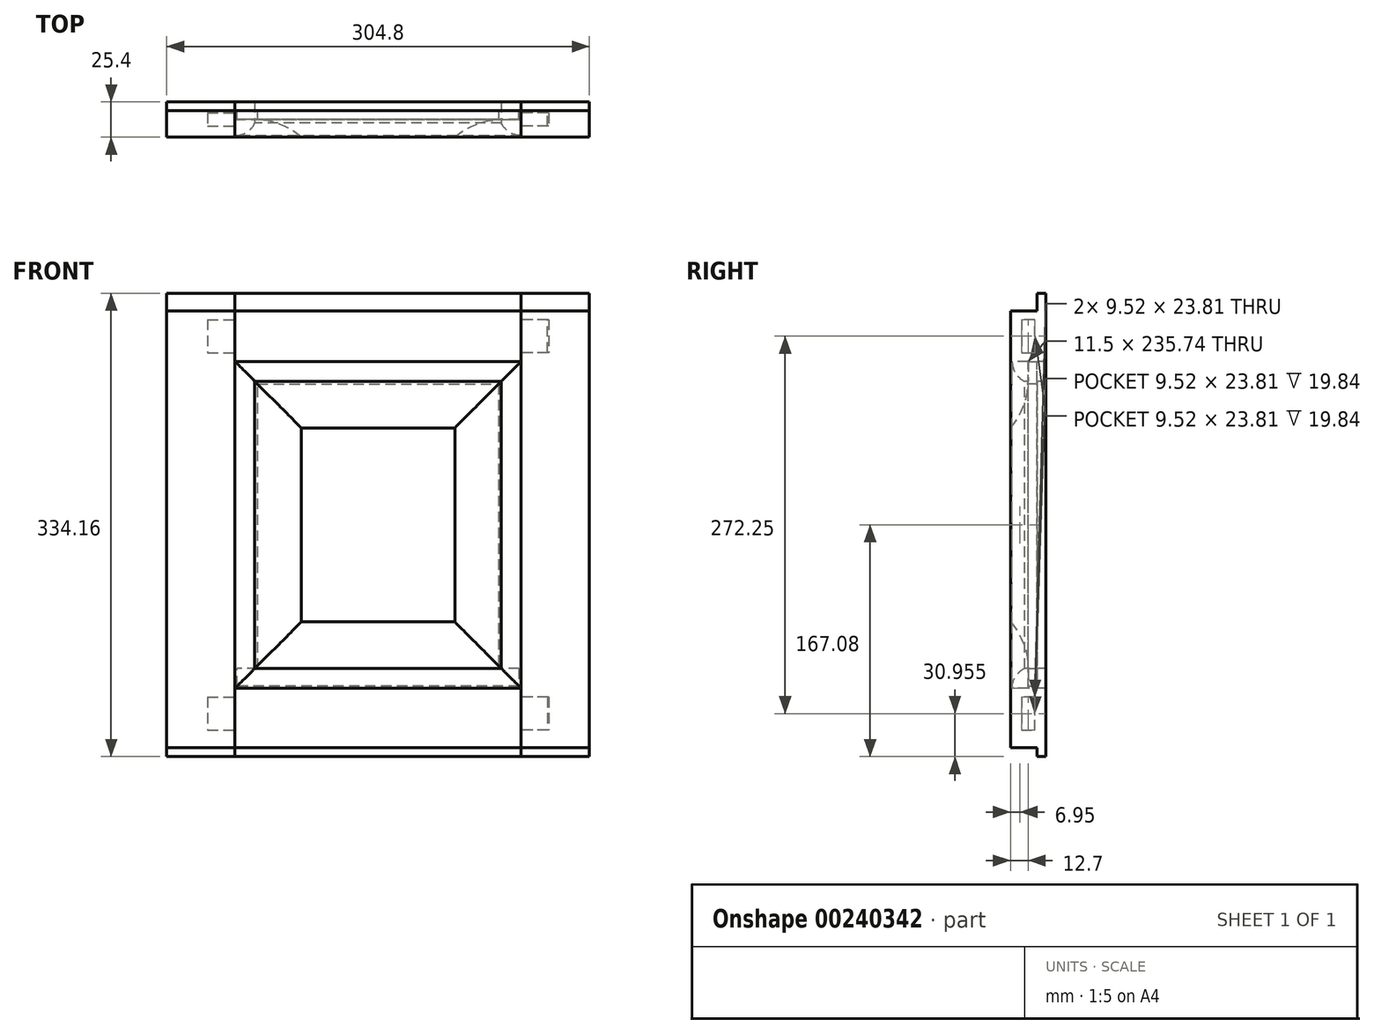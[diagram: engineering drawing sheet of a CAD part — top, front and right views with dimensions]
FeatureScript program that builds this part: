
annotation { "Feature Type Name" : "Feature", "Feature Type Description" : "" }
export const myFeature = defineFeature(function(context is Context, id is Id, definition is map)
    precondition{}
    {
        {
            var Q0;
            Q0=qCreatedBy(makeId("Front.planeOp"),FACE);
            var sketch = newSketch(context, id + "F0", { "sketchPlane" : qUnion([Q0])});
            skLineSegment(sketch, "E0.bottom", {"start": v(88.9, 103.58) * mm, "end": v(-88.9, 103.58) * mm});
            skLineSegment(sketch, "E1", {"start": v(-88.9, 103.58) * mm, "end": v(-103.19, 117.87) * mm});
            skLineSegment(sketch, "E2", {"start": v(-103.19, 117.87) * mm, "end": v(-103.19, 167.08) * mm});
            skLineSegment(sketch, "E3", {"start": v(-103.19, 167.08) * mm, "end": v(111.13, 167.08) * mm});
            skLineSegment(sketch, "E4.MirrorCS", {"start": v(-88.9, -103.58) * mm, "end": v(-103.19, -117.87) * mm});
            skLineSegment(sketch, "E5.MirrorCS", {"start": v(88.9, -103.58) * mm, "end": v(-88.9, -103.58) * mm});
            skLineSegment(sketch, "E6.MirrorCS", {"start": v(-103.19, -167.08) * mm, "end": v(111.13, -167.08) * mm});
            skLineSegment(sketch, "E7.MirrorCS", {"start": v(-103.19, -117.87) * mm, "end": v(-103.19, -167.08) * mm});
            skLineSegment(sketch, "E8", {"start": v(-103.19, 167.08) * mm, "end": v(-152.4, 167.08) * mm});
            skLineSegment(sketch, "E9", {"start": v(-152.4, 167.08) * mm, "end": v(-152.4, -167.08) * mm});
            skLineSegment(sketch, "E10", {"start": v(-152.4, -167.08) * mm, "end": v(-103.19, -167.08) * mm});
            skLineSegment(sketch, "E11", {"start": v(-88.9, 103.58) * mm, "end": v(-88.9, -103.58) * mm});
            skLineSegment(sketch, "E12.MirrorCS", {"start": v(88.9, -103.58) * mm, "end": v(103.19, -117.87) * mm});
            skLineSegment(sketch, "E13.MirrorCS", {"start": v(103.19, 117.87) * mm, "end": v(103.19, 167.08) * mm});
            skLineSegment(sketch, "E14.MirrorCS", {"start": v(103.19, -117.87) * mm, "end": v(103.19, -167.08) * mm});
            skLineSegment(sketch, "E15.MirrorCS", {"start": v(152.4, 167.08) * mm, "end": v(152.4, -167.08) * mm});
            skLineSegment(sketch, "E16.MirrorCS", {"start": v(152.4, -167.08) * mm, "end": v(103.19, -167.08) * mm});
            skLineSegment(sketch, "E17.MirrorCS", {"start": v(103.19, 167.08) * mm, "end": v(152.4, 167.08) * mm});
            skLineSegment(sketch, "E18.MirrorCS", {"start": v(88.9, 103.58) * mm, "end": v(88.9, -103.58) * mm});
            skLineSegment(sketch, "E19", {"start": v(88.9, 103.58) * mm, "end": v(103.19, 117.87) * mm});
            skSolve(sketch);
        }
        {
            var Q0;
            Q0=makeQuery(id+"F0.imprint","IMPRINT",FACE,{"disambiguationData":[TD([[makeQuery(id+"F0.imprint","IMPRINT",EDGE,{"derivedFrom":sQuery(id+"F0.wireOp",EDGE,"E0.bottom")}),-1.0]])]});
            extrude(context, id + "F1", {"entities" : qUnion([Q0]), "oppositeDirection" : true, "depth" : 25.4 * mm});
        }
        {
            var Q0;
            Q0=makeQuery(id+"F1.opExtrude","SWEPT_FACE",FACE,{"disambiguationData":[OSD([sQuery(id+"F0.wireOp",EDGE,"E2")])]});
            var sketch = newSketch(context, id + "F2", { "sketchPlane" : qUnion([Q0])});
            skLineSegment(sketch, "E20.bottom", {"start": v(-7.94, 124.22) * mm, "end": v(-17.46, 124.22) * mm});
            skLineSegment(sketch, "E20.top", {"start": v(-7.94, 148.03) * mm, "end": v(-17.46, 148.03) * mm});
            skLineSegment(sketch, "E20.left", {"start": v(-7.94, 124.22) * mm, "end": v(-7.94, 148.03) * mm});
            skLineSegment(sketch, "E20.right", {"start": v(-17.46, 124.22) * mm, "end": v(-17.46, 148.03) * mm});
            skPoint(sketch, "E20.middle", {"position": v(-12.7, 136.13) * mm});
            skSolve(sketch);
        }
        {
            var Q0;
            Q0 = qSketchRegion(id + "F2", true);
            extrude(context, id + "F3", {"entities" : qUnion([Q0]), "depth" : 19.05 * mm});
        }
        {
            var Q0;
            Q0=makeQuery(id+"F3.opExtrude","SWEPT_BODY",BODY,{"disambiguationData":[OSD([sQuery(id+"F2.wireOp",EDGE,"E20.bottom"),sQuery(id+"F2.wireOp",EDGE,"E20.top"),sQuery(id+"F2.wireOp",EDGE,"E20.left"),sQuery(id+"F2.wireOp",EDGE,"E20.right")])]});
            var Q1;
            Q1=qCreatedBy(makeId("Right.planeOp"),FACE);
            mirror(context, id + "F4", {"operationType" : NewBodyOperationType.ADD, "entities" : qUnion([Q0]), "mirrorPlane" : qUnion([Q1])});
        }
        {
            var Q0;
            Q0=makeQuery(id+"F0.imprint","IMPRINT",FACE,{"disambiguationData":[TD([[makeQuery(id+"F0.imprint","IMPRINT",EDGE,{"derivedFrom":sQuery(id+"F0.wireOp",EDGE,"E1")}),1.0]])]});
            extrude(context, id + "F5", {"entities" : qUnion([Q0]), "oppositeDirection" : true, "depth" : 25.4 * mm});
        }
        {
            var Q0;
            Q0=makeQuery(id+"F1.opExtrude","SWEPT_BODY",BODY,{"disambiguationData":[OSD([sQuery(id+"F0.wireOp",EDGE,"E0.bottom"),sQuery(id+"F0.wireOp",EDGE,"E1"),sQuery(id+"F0.wireOp",EDGE,"E2"),sQuery(id+"F0.wireOp",EDGE,"E3"),sQuery(id+"F0.wireOp",EDGE,"6457b620-730b-450c-8f20-c046bc1b6dd80.MirrorCS"),sQuery(id+"F0.wireOp",EDGE,"E13.MirrorCS")])]});
            var Q1;
            Q1=qCreatedBy(makeId("Top.planeOp"),FACE);
            mirror(context, id + "F6", {"entities" : qUnion([Q0]), "mirrorPlane" : qUnion([Q1])});
        }
        {
            var Q0;
            Q0=makeQuery(id+"F5.opExtrude","SWEPT_FACE",FACE,{"disambiguationData":[OSD([sQuery(id+"F0.wireOp",EDGE,"E11")])]});
            var sketch = newSketch(context, id + "F7", { "sketchPlane" : qUnion([Q0])});
            skLineSegment(sketch, "E21.0", {"start": v(19.05, 117.87) * mm, "end": v(19.05, -117.87) * mm});
            skLineSegment(sketch, "E22.0", {"start": v(19.05, 117.87) * mm, "end": v(12.7, 117.87) * mm});
            skLineSegment(sketch, "E23.0", {"start": v(19.05, -117.87) * mm, "end": v(12.7, -117.87) * mm});
            skLineSegment(sketch, "E24", {"start": v(12.7, -117.87) * mm, "end": v(12.7, 117.87) * mm});
            skSolve(sketch);
        }
        {
            var Q0;
            Q0=makeQuery(id+"F5.opExtrude","SWEPT_FACE",FACE,{"disambiguationData":[OSD([sQuery(id+"F0.wireOp",EDGE,"E7.MirrorCS")])]});
            var sketch = newSketch(context, id + "F8", { "sketchPlane" : qUnion([Q0])});
            skLineSegment(sketch, "E25.0.0", {"start": v(7.94, 148.03) * mm, "end": v(7.94, 124.22) * mm});
            skLineSegment(sketch, "E25.0.1", {"start": v(7.94, 124.22) * mm, "end": v(17.46, 124.22) * mm});
            skLineSegment(sketch, "E25.0.2", {"start": v(17.46, 124.22) * mm, "end": v(17.46, 148.03) * mm});
            skLineSegment(sketch, "E25.0.3", {"start": v(17.46, 148.03) * mm, "end": v(7.94, 148.03) * mm});
            skLineSegment(sketch, "E26.0.0", {"start": v(7.94, -124.22) * mm, "end": v(7.94, -148.03) * mm});
            skLineSegment(sketch, "E26.0.1", {"start": v(7.94, -148.03) * mm, "end": v(17.46, -148.03) * mm});
            skLineSegment(sketch, "E26.0.2", {"start": v(17.46, -148.03) * mm, "end": v(17.46, -124.22) * mm});
            skLineSegment(sketch, "E26.0.3", {"start": v(17.46, -124.22) * mm, "end": v(7.94, -124.22) * mm});
            skSolve(sketch);
        }
        {
            var Q0;
            Q0 = qSketchRegion(id + "F8", true);
            extrude(context, id + "F9", {"entities" : qUnion([Q0]), "operationType" : NewBodyOperationType.REMOVE, "oppositeDirection" : true, "depth" : 19.84 * mm});
        }
        {
            var Q0;
            Q0=qCreatedBy(makeId("Top.planeOp"),FACE);
            var sketch = newSketch(context, id + "F10", { "sketchPlane" : qUnion([Q0])});
            skLineSegment(sketch, "E27.0", {"start": v(-86.89, 19.05) * mm, "end": v(-103.19, 19.05) * mm});
            skLineSegment(sketch, "E28", {"start": v(-103.19, 19.05) * mm, "end": v(-103.19, 12.7) * mm});
            skPoint(sketch, "E28.startSnap0", {"position": v(-92.07, 19.05) * mm});
            skLineSegment(sketch, "E29", {"start": v(-103.19, 12.7) * mm, "end": v(-86.89, 12.7) * mm});
            skLineSegment(sketch, "E30", {"start": v(-86.89, 12.7) * mm, "end": v(-86.89, 19.05) * mm});
            skPoint(sketch, "E31.orphan", {"position": v(-95.25, 19.05) * mm});
            skPoint(sketch, "E32.orphan", {"position": v(-88.9, 19.05) * mm});
            skSolve(sketch);
        }
        {
            var Q0;
            Q0 = qSketchRegion(id + "F10", true);
            var Q1;
            Q1=makeQuery(id+"F5.opExtrude","SWEPT_FACE",FACE,{"disambiguationData":[OSD([sQuery(id+"F0.wireOp",EDGE,"E4.MirrorCS")])]});
            extrude(context, id + "F11", {"entities" : qUnion([Q0]), "operationType" : NewBodyOperationType.REMOVE, "endBound" : BoundingType.UP_TO_SURFACE, "oppositeDirection" : true, "endBoundEntityFace" : qUnion([Q1]), "depth" : 25.4 * mm});
        }
        {
            var Q0;
            Q0=makeQuery(id+"F5.opExtrude","SWEPT_BODY",BODY,{"disambiguationData":[OSD([sQuery(id+"F0.wireOp",EDGE,"E1"),sQuery(id+"F0.wireOp",EDGE,"E2"),sQuery(id+"F0.wireOp",EDGE,"E4.MirrorCS"),sQuery(id+"F0.wireOp",EDGE,"E7.MirrorCS"),sQuery(id+"F0.wireOp",EDGE,"E8"),sQuery(id+"F0.wireOp",EDGE,"E9"),sQuery(id+"F0.wireOp",EDGE,"E10"),sQuery(id+"F0.wireOp",EDGE,"E11")])]});
            var Q1;
            Q1=qCreatedBy(makeId("Right.planeOp"),FACE);
            mirror(context, id + "F12", {"entities" : qUnion([Q0]), "mirrorPlane" : qUnion([Q1])});
        }
        {
            var Q0;
            Q0=qCreatedBy(makeId("Top.planeOp"),FACE);
            var sketch = newSketch(context, id + "F13", { "sketchPlane" : qUnion([Q0])});
            skLineSegment(sketch, "E33.0", {"start": v(-88.9, -0.4) * mm, "end": v(-103.19, -0.4) * mm});
            skLineSegment(sketch, "E34.0", {"start": v(-103.19, 19.05) * mm, "end": v(-103.19, -0.4) * mm});
            skPoint(sketch, "E35.orphan", {"position": v(-103.19, 12.7) * mm});
            skLineSegment(sketch, "E36.0", {"start": v(-88.9, 12.7) * mm, "end": v(-88.9, -0.4) * mm});
            skPoint(sketch, "E37.orphan", {"position": v(-88.9, 0) * mm});
            skLineSegment(sketch, "E38", {"start": v(-103.19, 1.2) * mm, "end": v(-106.37, 1.2) * mm, "construction": true});
            skArc(sketch, "E39", {"start": v(-103.19, 1.2) * mm, "mid": v(-94.76, 3.61) * mm, "end": v(-88.9, 10.15) * mm});
            skSolve(sketch);
        }
        {
            var Q0;
            Q0 = qSketchRegion(id + "F13", true);
            var Q1;
            Q1=makeQuery(id+"F5.opExtrude","CAP_EDGE",EDGE,{"disambiguationData":[OSD([sQuery(id+"F0.wireOp",EDGE,"E11")])],"isStart":true});
            var Q2;
            Q2=makeQuery(id+"F1.opExtrude","CAP_EDGE",EDGE,{"disambiguationData":[OSD([sQuery(id+"F0.wireOp",EDGE,"E0.bottom")])],"isStart":true});
            var Q3;
            Q3=makeQuery(id+"F12.opPattern","COPY",EDGE,{"derivedFrom":makeQuery(id+"F5.opExtrude","CAP_EDGE",EDGE,{"disambiguationData":[OSD([sQuery(id+"F0.wireOp",EDGE,"E11")])],"isStart":true}),"instanceName":"1"});
            var Q4;
            Q4=makeQuery(id+"F6.opPattern","COPY",EDGE,{"derivedFrom":makeQuery(id+"F1.opExtrude","CAP_EDGE",EDGE,{"disambiguationData":[OSD([sQuery(id+"F0.wireOp",EDGE,"E0.bottom")])],"isStart":true}),"instanceName":"1"});
            sweep(context, id + "F14", {"operationType" : NewBodyOperationType.REMOVE, "profiles" : qUnion([Q0]), "path" : qUnion([Q1, Q2, Q3, Q4])});
        }
        {
            var Q0;
            Q0=qCreatedBy(makeId("Top.planeOp"),FACE);
            var sketch = newSketch(context, id + "F15", { "sketchPlane" : qUnion([Q0])});
            skLineSegment(sketch, "E40", {"start": v(-55.3, 0) * mm, "end": v(0, 0) * mm});
            skLineSegment(sketch, "E41.0", {"start": v(-101.6, 19.05) * mm, "end": v(-101.6, 12.7) * mm});
            skLineSegment(sketch, "E42.0", {"start": v(-88.9, 12.7) * mm, "end": v(-101.6, 12.7) * mm});
            skArc(sketch, "E43", {"start": v(-88.9, 12.7) * mm, "mid": v(-70.94, 9.42) * mm, "end": v(-55.3, 0) * mm});
            skLineSegment(sketch, "E44.0", {"start": v(-88.9, 19.05) * mm, "end": v(0, 19.05) * mm});
            skPoint(sketch, "E45.orphan", {"position": v(-101.6, 19.05) * mm});
            skLineSegment(sketch, "E46.0", {"start": v(-101.6, 19.05) * mm, "end": v(-88.9, 19.05) * mm});
            skLineSegment(sketch, "E47", {"start": v(0, 0) * mm, "end": v(0, 19.05) * mm});
            skSolve(sketch);
        }
        {
            var Q0;
            Q0 = qSketchRegion(id + "F15", true);
            var Q1;
            Q1=makeQuery(id+"F5.opExtrude","CAP_EDGE",EDGE,{"disambiguationData":[OSD([sQuery(id+"F0.wireOp",EDGE,"E11")])],"isStart":false});
            var Q2;
            Q2=makeQuery(id+"F1.opExtrude","CAP_EDGE",EDGE,{"disambiguationData":[OSD([sQuery(id+"F0.wireOp",EDGE,"E0.bottom")])],"isStart":false});
            var Q3;
            Q3=makeQuery(id+"F12.opPattern","COPY",EDGE,{"derivedFrom":makeQuery(id+"F5.opExtrude","CAP_EDGE",EDGE,{"disambiguationData":[OSD([sQuery(id+"F0.wireOp",EDGE,"E11")])],"isStart":false}),"instanceName":"1"});
            var Q4;
            Q4=makeQuery(id+"F6.opPattern","COPY",EDGE,{"derivedFrom":makeQuery(id+"F1.opExtrude","CAP_EDGE",EDGE,{"disambiguationData":[OSD([sQuery(id+"F0.wireOp",EDGE,"E0.bottom")])],"isStart":false}),"instanceName":"1"});
            sweep(context, id + "F16", {"profiles" : qUnion([Q0]), "path" : qUnion([Q1, Q2, Q3, Q4])});
        }
        {
            var Q0;
            Q0=makeQuery(id+"F1.opExtrude","SWEPT_FACE",FACE,{"disambiguationData":[OSD([sQuery(id+"F0.wireOp",EDGE,"E3")])]});
            var sketch = newSketch(context, id + "F17", { "sketchPlane" : qUnion([Q0])});
            skLineSegment(sketch, "E48.0", {"start": v(-152.4, 19.05) * mm, "end": v(152.4, 19.05) * mm});
            skLineSegment(sketch, "E49.0", {"start": v(-152.4, 19.05) * mm, "end": v(-152.4, 0) * mm});
            skLineSegment(sketch, "E50.0", {"start": v(152.4, 19.05) * mm, "end": v(152.4, 0) * mm});
            skLineSegment(sketch, "E51.0", {"start": v(-152.4, 0) * mm, "end": v(152.4, 0) * mm});
            skPoint(sketch, "E52.orphan", {"position": v(-103.19, 0) * mm});
            skPoint(sketch, "E53.orphan", {"position": v(103.19, 0) * mm});
            skPoint(sketch, "E54.orphan", {"position": v(-152.4, 25.4) * mm});
            skPoint(sketch, "E55.orphan", {"position": v(152.4, 25.4) * mm});
            skSolve(sketch);
        }
        {
            var Q0;
            Q0 = qSketchRegion(id + "F17", true);
            extrude(context, id + "F18", {"entities" : qUnion([Q0]), "operationType" : NewBodyOperationType.REMOVE, "oppositeDirection" : true, "depth" : 12.7 * mm});
        }
        {
            var Q0;
            Q0=makeQuery(id+"F6.opPattern","COPY",FACE,{"derivedFrom":makeQuery(id+"F1.opExtrude","SWEPT_FACE",FACE,{"disambiguationData":[OSD([sQuery(id+"F0.wireOp",EDGE,"E3")])]}),"instanceName":"1"});
            var sketch = newSketch(context, id + "F19", { "sketchPlane" : qUnion([Q0])});
            skLineSegment(sketch, "E56.0", {"start": v(-152.4, -19.05) * mm, "end": v(152.4, -19.05) * mm});
            skLineSegment(sketch, "E57.0", {"start": v(-152.4, 0) * mm, "end": v(152.4, 0) * mm});
            skLineSegment(sketch, "E58.0", {"start": v(-152.4, -19.05) * mm, "end": v(-152.4, 0) * mm});
            skLineSegment(sketch, "E59.0", {"start": v(152.4, -19.05) * mm, "end": v(152.4, 0) * mm});
            skPoint(sketch, "E60.orphan", {"position": v(-103.19, 0) * mm});
            skPoint(sketch, "E61.orphan", {"position": v(103.19, 0) * mm});
            skPoint(sketch, "E62.orphan", {"position": v(-152.4, -25.4) * mm});
            skPoint(sketch, "E63.orphan", {"position": v(152.4, -25.4) * mm});
            skSolve(sketch);
        }
        {
            var Q0;
            Q0 = qSketchRegion(id + "F19", true);
            extrude(context, id + "F20", {"entities" : qUnion([Q0]), "operationType" : NewBodyOperationType.REMOVE, "oppositeDirection" : true, "depth" : 6.35 * mm});
        }
        {
            var Q0;
            Q0 = qSketchRegion(id + "F10", true);
            var Q1;
            Q1=makeQuery(id+"F5.opExtrude","CAP_EDGE",EDGE,{"disambiguationData":[OSD([sQuery(id+"F0.wireOp",EDGE,"E11")])],"isStart":false});
            var Q2;
            Q2=makeQuery(id+"F1.opExtrude","CAP_EDGE",EDGE,{"disambiguationData":[OSD([sQuery(id+"F0.wireOp",EDGE,"E0.bottom")])],"isStart":false});
            var Q3;
            Q3=makeQuery(id+"F12.opPattern","COPY",EDGE,{"derivedFrom":makeQuery(id+"F5.opExtrude","CAP_EDGE",EDGE,{"disambiguationData":[OSD([sQuery(id+"F0.wireOp",EDGE,"E11")])],"isStart":false}),"instanceName":"1"});
            sweep(context, id + "F21", {"operationType" : NewBodyOperationType.REMOVE, "profiles" : qUnion([Q0]), "path" : qUnion([Q1, Q2, Q3])});
        }
        {
            var Q0;
            Q0=qCreatedBy(makeId("Right.planeOp"),FACE);
            var sketch = newSketch(context, id + "F22", { "sketchPlane" : qUnion([Q0])});
            skLineSegment(sketch, "E64.0", {"start": v(19.05, 117.87) * mm, "end": v(19.05, 103.58) * mm});
            skLineSegment(sketch, "E65.0", {"start": v(12.7, 103.58) * mm, "end": v(12.7, 117.87) * mm});
            skLineSegment(sketch, "E66.0", {"start": v(19.05, 103.58) * mm, "end": v(12.7, 103.58) * mm});
            skLineSegment(sketch, "E67.0", {"start": v(19.05, 117.87) * mm, "end": v(12.7, 117.87) * mm});
            skSolve(sketch);
        }
        {
            var Q0;
            Q0 = qSketchRegion(id + "F22", true);
            extrude(context, id + "F23", {"entities" : qUnion([Q0]), "operationType" : NewBodyOperationType.REMOVE, "endBound" : BoundingType.SYMMETRIC, "oppositeDirection" : true, "depth" : 206.38 * mm});
        }
    });
